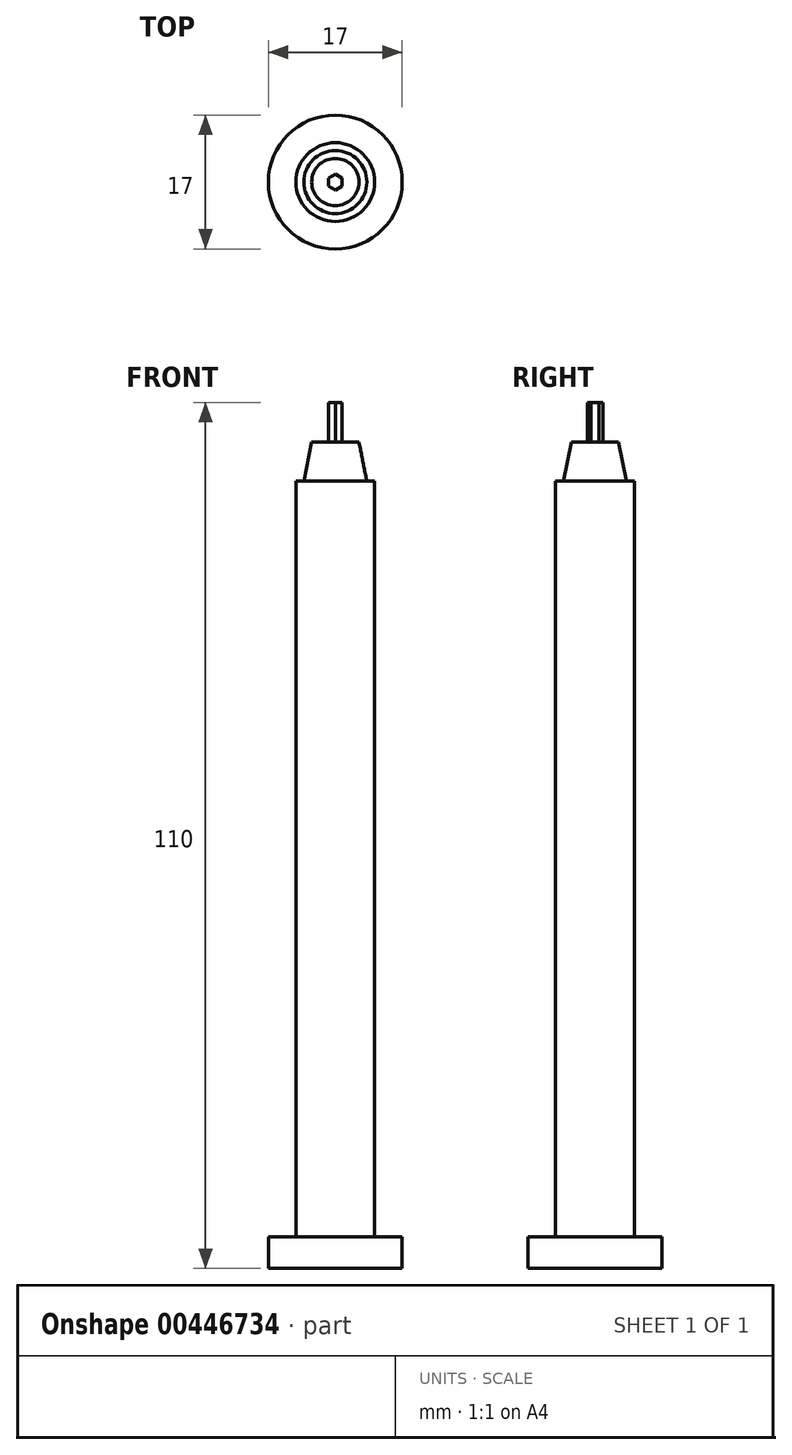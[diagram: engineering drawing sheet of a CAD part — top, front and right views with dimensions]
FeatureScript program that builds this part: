
annotation { "Feature Type Name" : "Feature", "Feature Type Description" : "" }
export const myFeature = defineFeature(function(context is Context, id is Id, definition is map)
    precondition{}
    {
        {
            var Q0;
            Q0=qCreatedBy(makeId("Top.planeOp"),FACE);
            var sketch = newSketch(context, id + "F0", { "sketchPlane" : qUnion([Q0])});
            skCircle(sketch, "E0", {"center": v(0, 0) * mm, "radius": 8.5 * mm});
            skSolve(sketch);
        }
        {
            var Q0;
            Q0=qSketchRegion(id+"F0",true);
            extrude(context, id + "F1", {"entities" : qUnion([Q0]), "depth" : 4 * mm});
        }
        {
            var Q0;
            Q0=qCreatedBy(makeId("Top.planeOp"),FACE);
            var sketch = newSketch(context, id + "F2", { "sketchPlane" : qUnion([Q0])});
            skCircle(sketch, "E1", {"center": v(0, 0) * mm, "radius": 5 * mm});
            skSolve(sketch);
        }
        {
            var Q0;
            Q0=qSketchRegion(id+"F2",true);
            extrude(context, id + "F3", {"entities" : qUnion([Q0]), "operationType" : NewBodyOperationType.ADD, "depth" : 100 * mm});
        }
        {
            var Q0;
            Q0=qCreatedBy(makeId("Right.planeOp"),FACE);
            var sketch = newSketch(context, id + "F4", { "sketchPlane" : qUnion([Q0])});
            skLineSegment(sketch, "E2", {"start": v(0, 105) * mm, "end": v(0, 100) * mm});
            skLineSegment(sketch, "E3", {"start": v(0, 100) * mm, "end": v(4, 100) * mm});
            skLineSegment(sketch, "E4", {"start": v(4, 100) * mm, "end": v(3, 105) * mm});
            skLineSegment(sketch, "E5", {"start": v(3, 105) * mm, "end": v(0, 105) * mm});
            skSolve(sketch);
        }
        {
            var Q0;
            Q0=makeQuery(id+"F4.imprint","IMPRINT",FACE,{"disambiguationData":[TD([[makeQuery(id+"F4.imprint","IMPRINT",EDGE,{"derivedFrom":sQuery(id+"F4.wireOp",EDGE,"E2")}),1.0]])]});
            var Q1;
            Q1=sQuery(id+"F4.wireOp",EDGE,"E2");
            revolve(context, id + "F5", {"operationType" : NewBodyOperationType.ADD, "entities" : qUnion([Q0]), "axis" : qUnion([Q1]), "revolveType" : RevolveType.FULL});
        }
        {
            var Q0;
            Q0=makeQuery(id+"F5.opRevolve","SWEPT_FACE",FACE,{"disambiguationData":[OSD([sQuery(id+"F4.wireOp",EDGE,"E5")])]});
            var sketch = newSketch(context, id + "F6", { "sketchPlane" : qUnion([Q0])});
            skCircle(sketch, "E6.cCircle", {"center": v(0, 0) * mm, "radius": 0.87 * mm, "construction": true});
            skLineSegment(sketch, "E6.0", {"start": v(0.87, 0.5) * mm, "end": v(0.87, -0.5) * mm});
            skLineSegment(sketch, "E6.1", {"start": v(0.87, -0.5) * mm, "end": v(0, -1) * mm});
            skLineSegment(sketch, "E6.2", {"start": v(0, -1) * mm, "end": v(-0.87, -0.5) * mm});
            skLineSegment(sketch, "E6.3", {"start": v(-0.87, -0.5) * mm, "end": v(-0.87, 0.5) * mm});
            skLineSegment(sketch, "E6.4", {"start": v(-0.87, 0.5) * mm, "end": v(0, 1) * mm});
            skLineSegment(sketch, "E6.5", {"start": v(0, 1) * mm, "end": v(0.87, 0.5) * mm});
            skPoint(sketch, "E6.0.midPoint", {"position": v(0.87, 0) * mm});
            skSolve(sketch);
        }
        {
            var Q0;
            Q0=makeQuery(id+"F6.imprint","IMPRINT",FACE,{"disambiguationData":[TD([[makeQuery(id+"F6.imprint","IMPRINT",EDGE,{"derivedFrom":sQuery(id+"F6.wireOp",EDGE,"E6.0")}),-1.0]])]});
            extrude(context, id + "F7", {"entities" : qUnion([Q0]), "operationType" : NewBodyOperationType.ADD, "depth" : 5 * mm});
        }
    });
